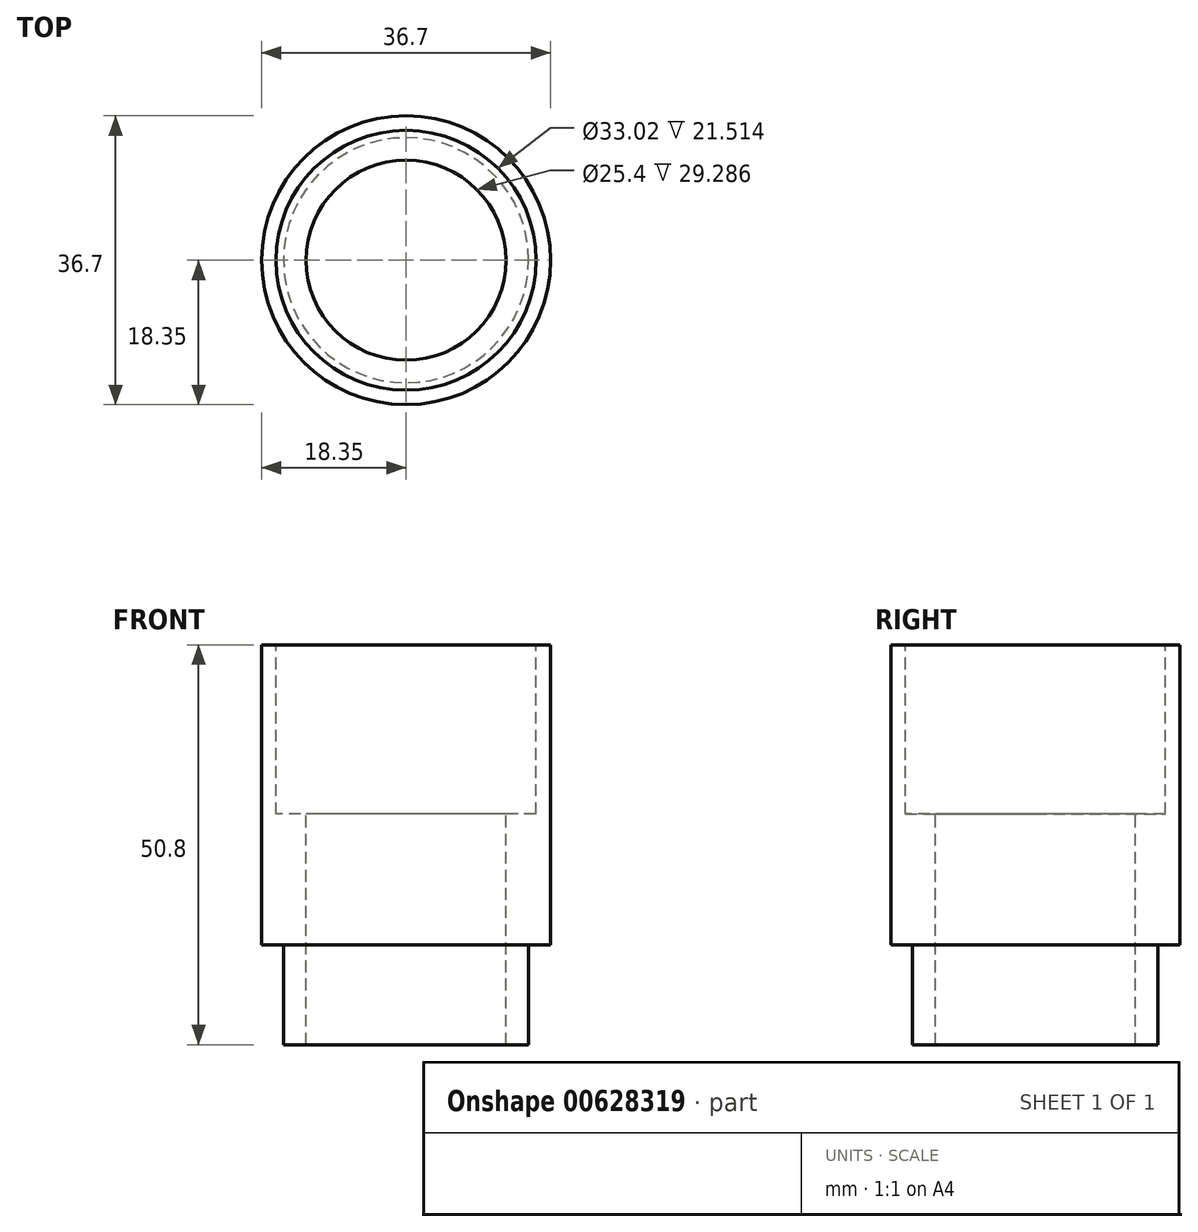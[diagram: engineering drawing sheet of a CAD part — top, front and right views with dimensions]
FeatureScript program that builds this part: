
annotation { "Feature Type Name" : "Feature", "Feature Type Description" : "" }
export const myFeature = defineFeature(function(context is Context, id is Id, definition is map)
    precondition{}
    {
        {
            var Q0;
            Q0=qCreatedBy(makeId("Front.planeOp"),FACE);
            var sketch = newSketch(context, id + "F0", { "sketchPlane" : qUnion([Q0])});
            skLineSegment(sketch, "E0.trimOffspring", {"start": v(18.35, -22.85) * mm, "end": v(18.35, 15.25) * mm});
            skLineSegment(sketch, "E1", {"start": v(0, 17.78) * mm, "end": v(0, -16.79) * mm});
            skLineSegment(sketch, "E2", {"start": v(18.35, 15.25) * mm, "end": v(16.51, 15.25) * mm});
            skLineSegment(sketch, "E3", {"start": v(16.51, 15.25) * mm, "end": v(16.51, -6.27) * mm});
            skLineSegment(sketch, "E4", {"start": v(16.51, -6.27) * mm, "end": v(12.7, -6.27) * mm});
            skLineSegment(sketch, "E5", {"start": v(12.7, -6.27) * mm, "end": v(12.7, -22.85) * mm});
            skLineSegment(sketch, "E6", {"start": v(15.57, -22.85) * mm, "end": v(18.35, -22.85) * mm});
            skLineSegment(sketch, "E7", {"start": v(12.7, -22.85) * mm, "end": v(12.7, -35.55) * mm});
            skLineSegment(sketch, "E8", {"start": v(12.7, -35.55) * mm, "end": v(15.57, -35.55) * mm});
            skLineSegment(sketch, "E9", {"start": v(15.57, -35.55) * mm, "end": v(15.57, -22.85) * mm});
            skSolve(sketch);
        }
        {
            var Q0;
            Q0=makeQuery(id+"F0.imprint","IMPRINT",FACE,{"disambiguationData":[TD([[makeQuery(id+"F0.imprint","IMPRINT",EDGE,{"derivedFrom":sQuery(id+"F0.wireOp",EDGE,"E0.trimOffspring")}),1.0]])]});
            var Q1;
            Q1=sQuery(id+"F0.wireOp",EDGE,"E1");
            revolve(context, id + "F1", {"entities" : qUnion([Q0]), "axis" : qUnion([Q1]), "revolveType" : RevolveType.FULL});
        }
    });
